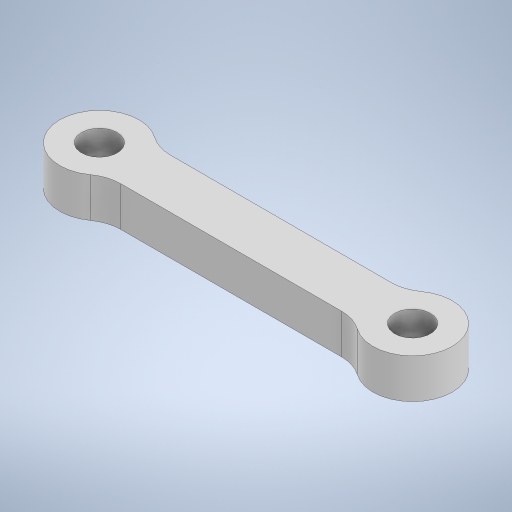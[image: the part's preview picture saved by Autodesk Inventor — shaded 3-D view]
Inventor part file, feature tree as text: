
AUTODESK INVENTOR PART (.ipt)
format: ipt  version: 2024.1 (Build 281209000, 209)  size: 262,144 bytes
history: native  units: in
note: dims shown in document units (in); Inventor stores cm internally (conversion verified against a paired STEP export)
features: extrude x1, fillet x1, direct_edit x1, sketch x1, other x1
ambient origin geometry x8: Origin, YZ Plane, XZ Plane, XY Plane, X Axis, Y Axis, Z Axis, Center Point
bodies: Solid1 (feature_tree)
feature tree (5):
  extrude  "Extrusion1"  Depth=0.3937in
  fillet  "Fillet1"  Radius=3.5433in
  direct_edit  "Direct Edit1"
  sketch  "Sketch1"  dims[d0=4.9213in d1=3.5433in d2=3.5433in d3=15.5512in d4=15.5512in d5=7.874in d6=7.874in d7=3.937in d8=0.0in d9=3.937in d10=0.0394in d11=0.3937in d12=0.3937in]
  other  "Scale1"
